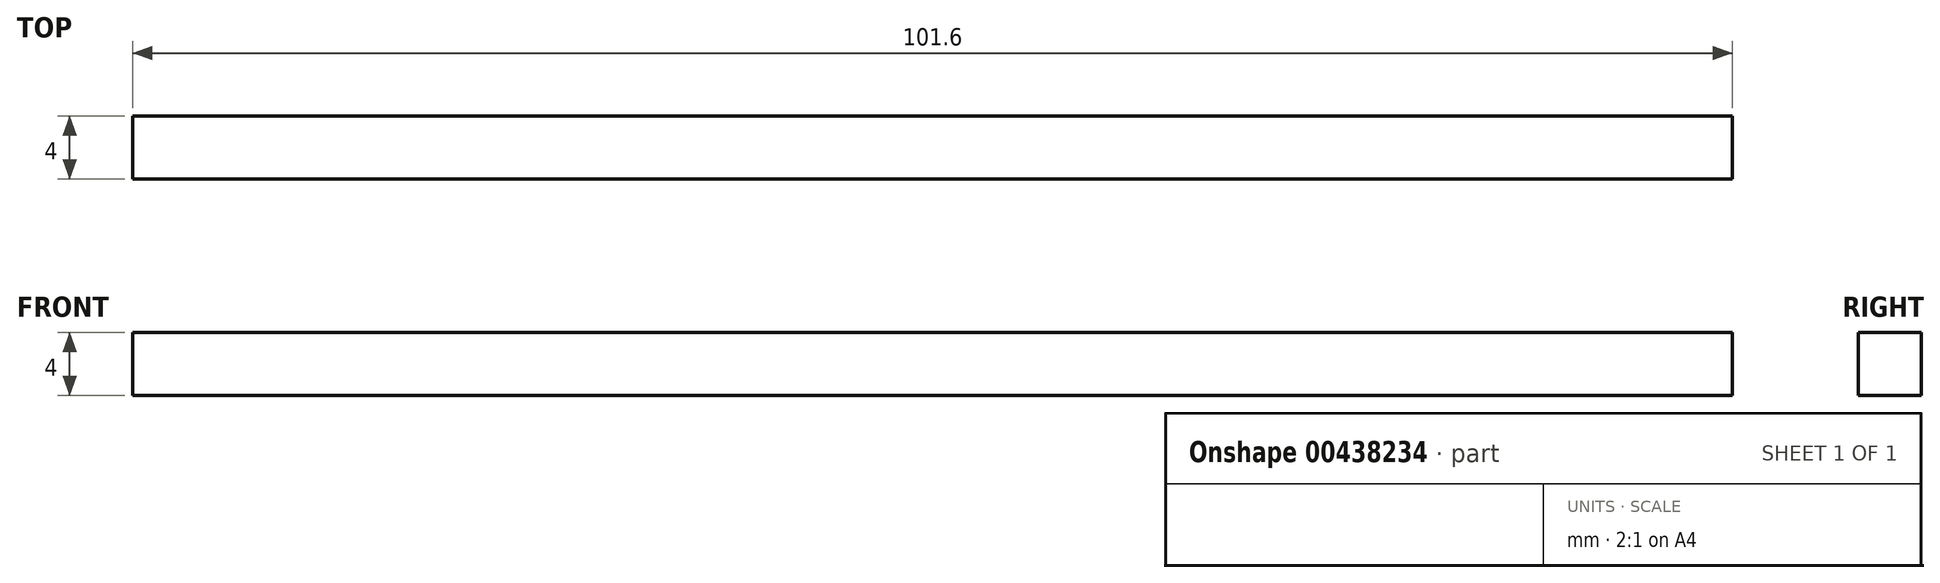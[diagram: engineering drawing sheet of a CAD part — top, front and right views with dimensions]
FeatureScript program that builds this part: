
annotation { "Feature Type Name" : "Feature", "Feature Type Description" : "" }
export const myFeature = defineFeature(function(context is Context, id is Id, definition is map)
    precondition{}
    {
        {
            var Q0;
            Q0=qCreatedBy(makeId("Front.planeOp"),FACE);
            var sketch = newSketch(context, id + "F0", { "sketchPlane" : qUnion([Q0])});
            skLineSegment(sketch, "E0", {"start": v(-68.4, 12.58) * mm, "end": v(33.2, 12.58) * mm});
            skLineSegment(sketch, "E1", {"start": v(33.2, 12.58) * mm, "end": v(33.2, 8.58) * mm});
            skLineSegment(sketch, "E2", {"start": v(33.2, 8.58) * mm, "end": v(-68.4, 8.58) * mm});
            skLineSegment(sketch, "E3", {"start": v(-68.4, 8.58) * mm, "end": v(-68.4, 12.58) * mm});
            skSolve(sketch);
        }
        {
            var Q0;
            Q0 = qSketchRegion(id + "F0", true);
            extrude(context, id + "F1", {"entities" : qUnion([Q0]), "depth" : 4 * mm, "offsetDistance" : 25.4 * mm});
        }
    });
